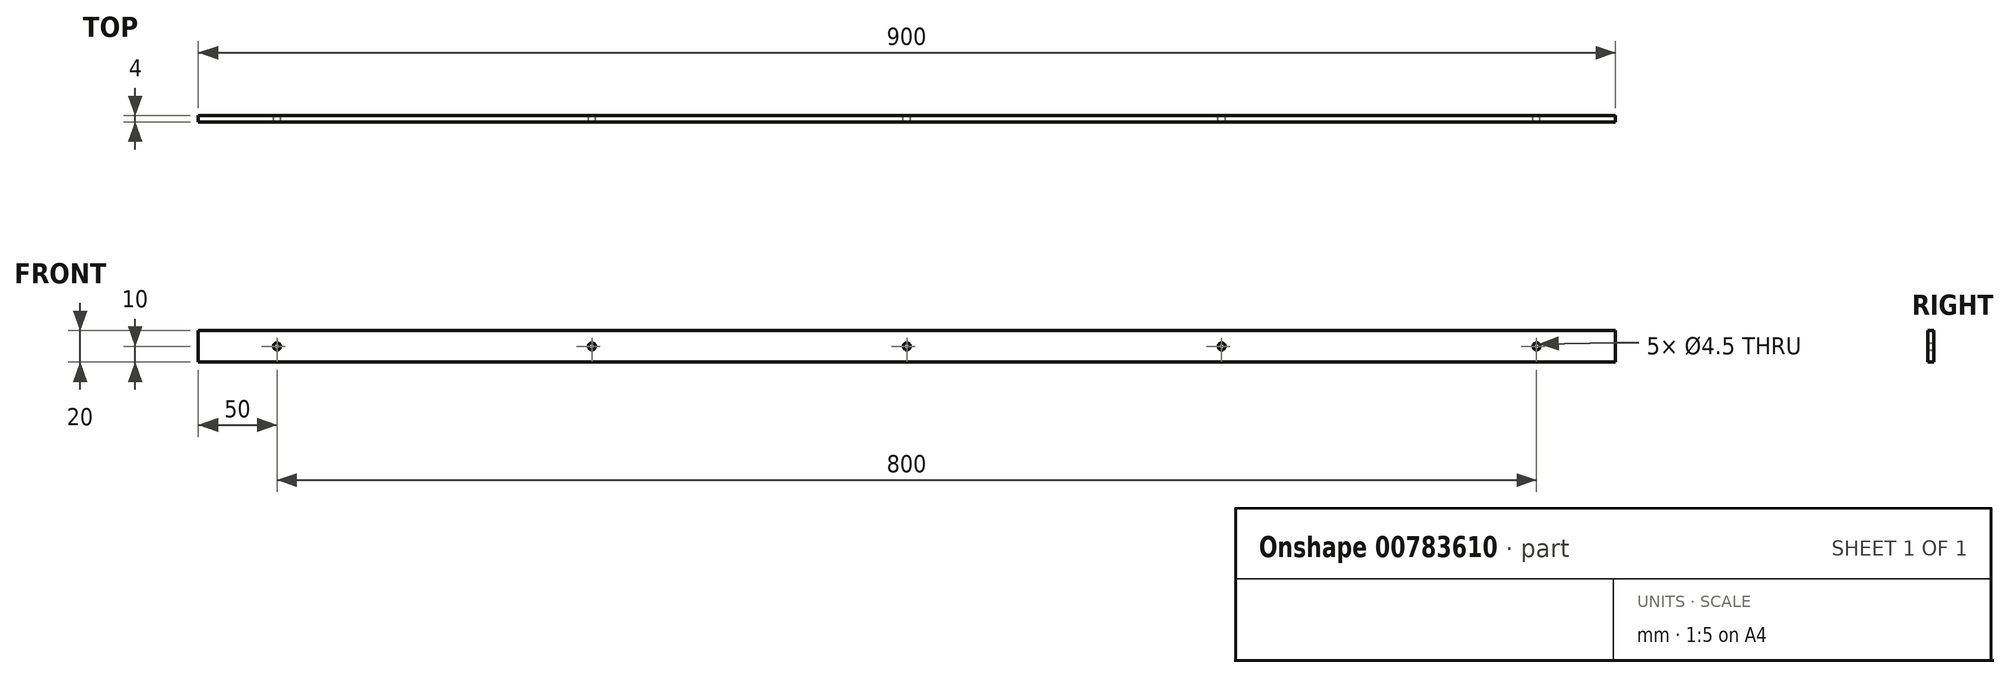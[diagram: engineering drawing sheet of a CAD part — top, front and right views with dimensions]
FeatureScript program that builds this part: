
annotation { "Feature Type Name" : "Feature", "Feature Type Description" : "" }
export const myFeature = defineFeature(function(context is Context, id is Id, definition is map)
    precondition{}
    {
        {
            var Q0;
            Q0=qCreatedBy(makeId("Front.planeOp"),FACE);
            var sketch = newSketch(context, id + "F0", { "sketchPlane" : qUnion([Q0])});
            skLineSegment(sketch, "E0.bottom", {"start": v(-450, 10) * mm, "end": v(450, 10) * mm});
            skLineSegment(sketch, "E0.top", {"start": v(-450, -10) * mm, "end": v(450, -10) * mm});
            skLineSegment(sketch, "E0.left", {"start": v(-450, 10) * mm, "end": v(-450, -10) * mm});
            skLineSegment(sketch, "E0.right", {"start": v(450, 10) * mm, "end": v(450, -10) * mm});
            skPoint(sketch, "E0.middle", {"position": v(0, 0) * mm});
            skLineSegment(sketch, "E1", {"start": v(-450, 0) * mm, "end": v(450, 0) * mm, "construction": true});
            skCircle(sketch, "E2", {"center": v(-400, 0) * mm, "radius": 2.25 * mm});
            skCircle(sketch, "E3.1.0.0", {"center": v(-200, 0) * mm, "radius": 2.25 * mm});
            skCircle(sketch, "E3.2.0.0", {"center": v(0, 0) * mm, "radius": 2.25 * mm});
            skCircle(sketch, "E3.3.0.0", {"center": v(200, 0) * mm, "radius": 2.25 * mm});
            skCircle(sketch, "E3.4.0.0", {"center": v(400, 0) * mm, "radius": 2.25 * mm});
            skLineSegment(sketch, "E3.direction1", {"start": v(-400, 0) * mm, "end": v(-200, 0) * mm, "construction": true});
            skSolve(sketch);
        }
        {
            var Q0;
            Q0=makeQuery(id+"F0.imprint","IMPRINT",FACE,{"disambiguationData":[TD([[makeQuery(id+"F0.imprint","IMPRINT",EDGE,{"derivedFrom":sQuery(id+"F0.wireOp",EDGE,"E0.bottom")}),-1.0]])]});
            extrude(context, id + "F1", {"entities" : qUnion([Q0]), "depth" : 4 * mm, "offsetDistance" : 25 * mm});
        }
    });
